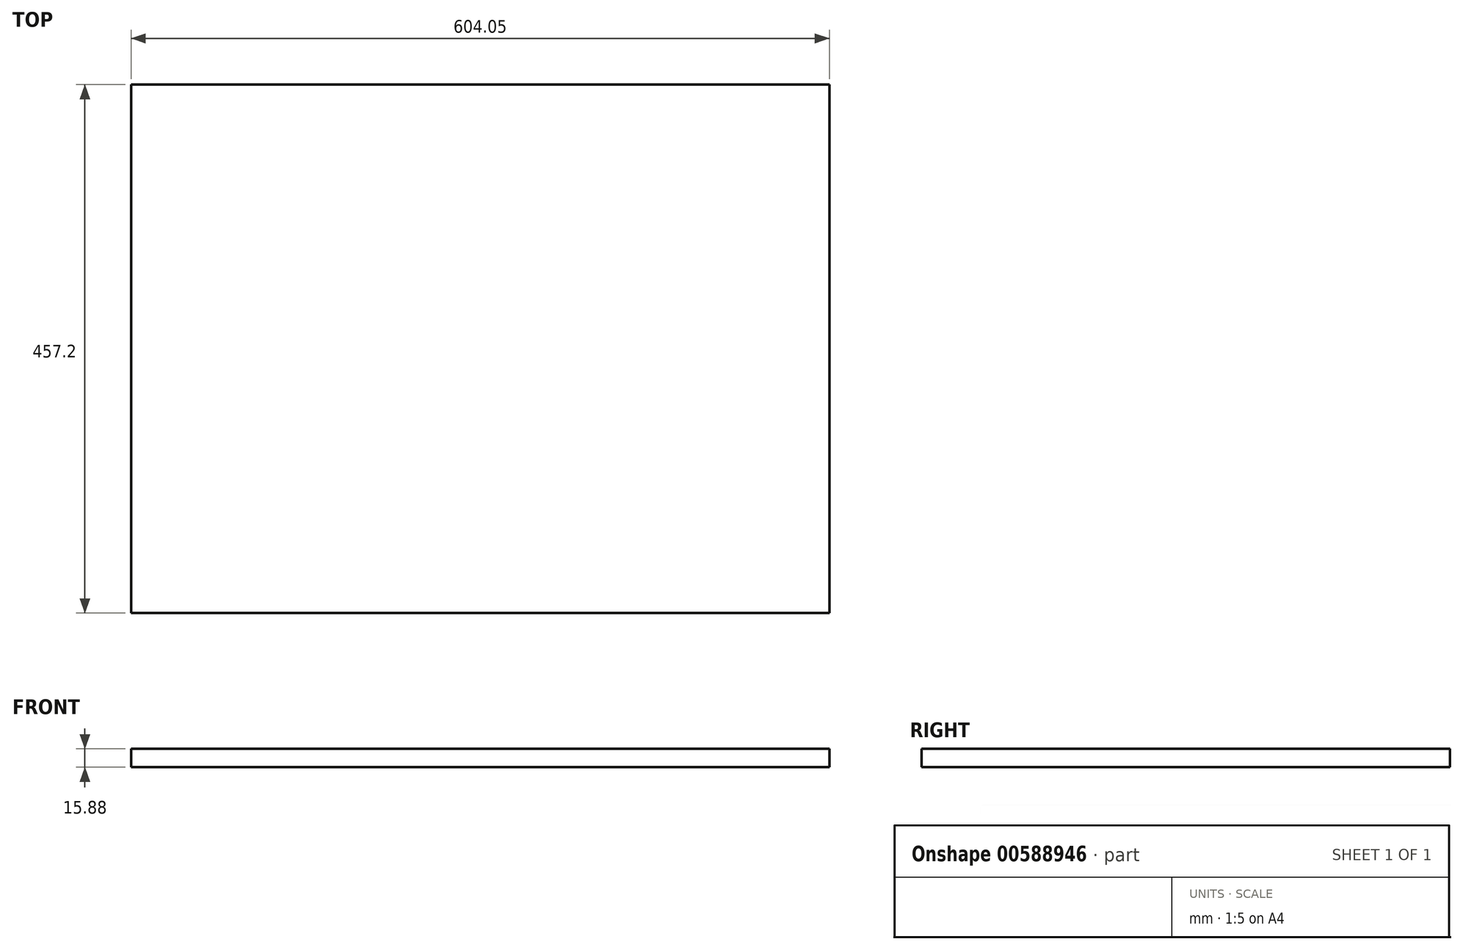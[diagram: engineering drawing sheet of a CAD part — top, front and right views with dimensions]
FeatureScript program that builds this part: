
annotation { "Feature Type Name" : "Feature", "Feature Type Description" : "" }
export const myFeature = defineFeature(function(context is Context, id is Id, definition is map)
    precondition{}
    {
        {
            var Q0;
            Q0=qCreatedBy(makeId("Top.planeOp"),FACE);
            var sketch = newSketch(context, id + "F0", { "sketchPlane" : qUnion([Q0])});
            skLineSegment(sketch, "E0.bottom", {"start": v(0, 0) * mm, "end": v(604.05, 0) * mm});
            skLineSegment(sketch, "E0.top", {"start": v(0, 457.2) * mm, "end": v(604.05, 457.2) * mm});
            skLineSegment(sketch, "E0.left", {"start": v(0, 0) * mm, "end": v(0, 457.2) * mm});
            skLineSegment(sketch, "E0.right", {"start": v(604.05, 0) * mm, "end": v(604.05, 457.2) * mm});
            skSolve(sketch);
        }
        {
            var Q0;
            Q0=makeQuery(id+"F0.imprint","IMPRINT",FACE,{"disambiguationData":[TD([[makeQuery(id+"F0.imprint","IMPRINT",EDGE,{"derivedFrom":sQuery(id+"F0.wireOp",EDGE,"E0.bottom")}),1.0]])]});
            extrude(context, id + "F1", {"entities" : qUnion([Q0]), "oppositeDirection" : true, "depth" : 15.88 * mm, "offsetDistance" : 25.4 * mm});
        }
    });
